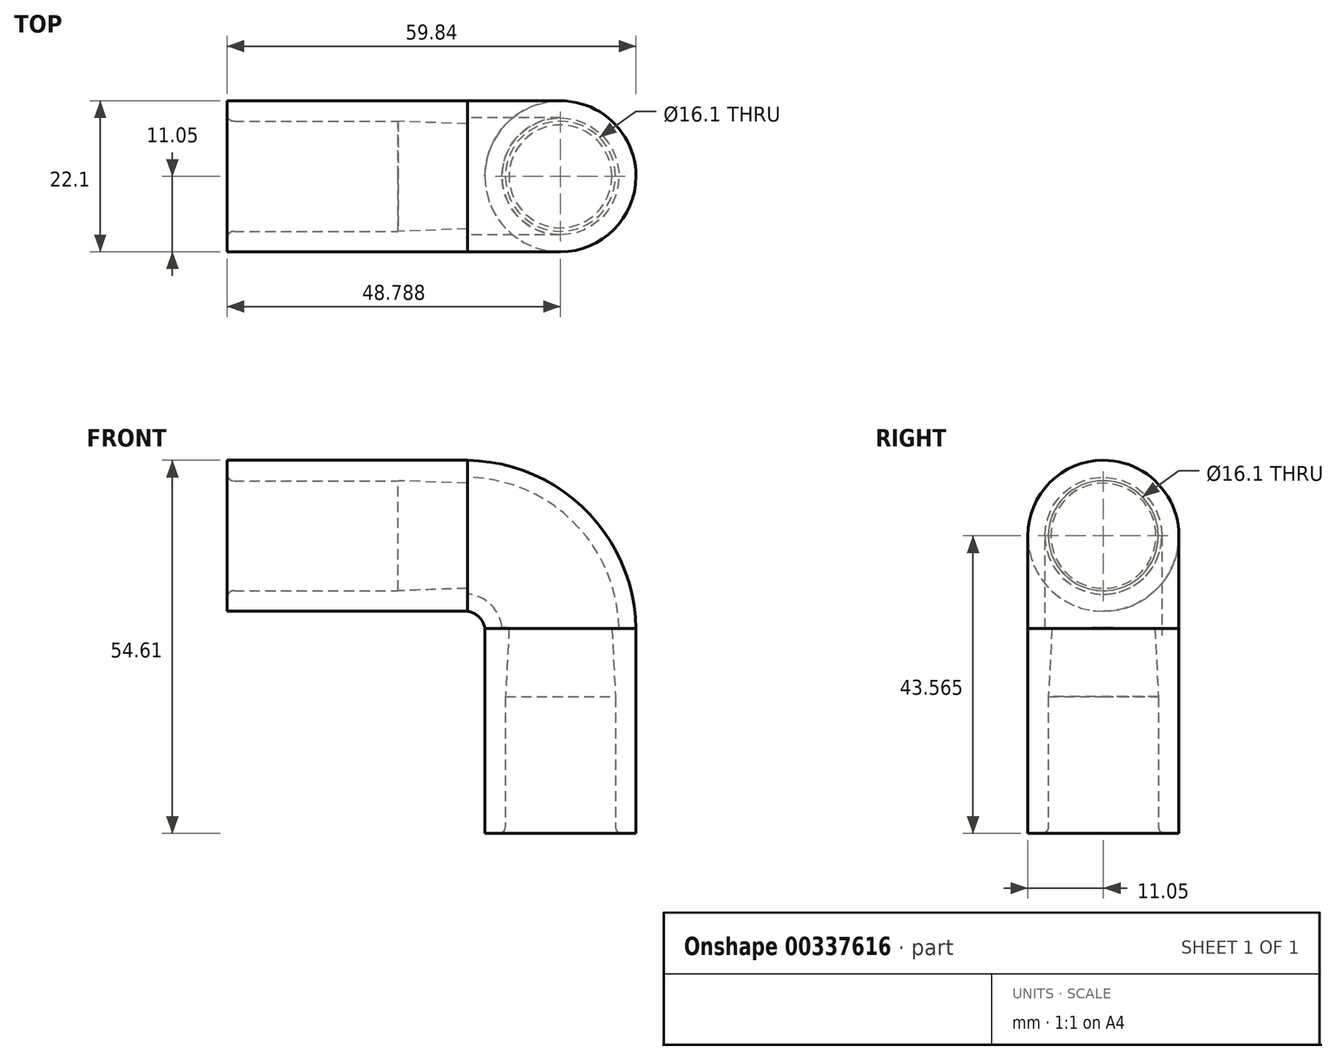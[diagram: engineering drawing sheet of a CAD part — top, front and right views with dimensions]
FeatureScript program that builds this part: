
annotation { "Feature Type Name" : "Feature", "Feature Type Description" : "" }
export const myFeature = defineFeature(function(context is Context, id is Id, definition is map)
    precondition{}
    {
        {
            var Q0;
            Q0=qCreatedBy(makeId("Front.planeOp"),FACE);
            var sketch = newSketch(context, id + "F0", { "sketchPlane" : qUnion([Q0])});
            skLineSegment(sketch, "E0", {"start": v(-11.93, -0.1) * mm, "end": v(-16.93, -0.1) * mm});
            skLineSegment(sketch, "E1", {"start": v(18.23, 2.9) * mm, "end": v(-16.93, 2.9) * mm});
            skLineSegment(sketch, "E2", {"start": v(-16.93, 2.9) * mm, "end": v(-16.93, -0.1) * mm});
            skLineSegment(sketch, "E3", {"start": v(36.1, -8.15) * mm, "end": v(3.24, -8.15) * mm, "construction": true});
            skLineSegment(sketch, "E4", {"start": v(8.07, -0.1) * mm, "end": v(-11.93, -0.1) * mm});
            skLineSegment(sketch, "E5", {"start": v(18.23, 2.9) * mm, "end": v(18.23, -0.45) * mm});
            skLineSegment(sketch, "E6", {"start": v(18.23, -0.45) * mm, "end": v(8.07, -0.1) * mm});
            skSolve(sketch);
        }
        {
            var Q0;
            Q0=makeQuery(id+"F0.imprint","IMPRINT",FACE,{"disambiguationData":[TD([[makeQuery(id+"F0.imprint","IMPRINT",EDGE,{"derivedFrom":sQuery(id+"F0.wireOp",EDGE,"E0")}),-1.0]])]});
            var Q1;
            Q1=sQuery(id+"F0.wireOp",EDGE,"E3");
            revolve(context, id + "F1", {"entities" : qUnion([Q0]), "axis" : qUnion([Q1]), "revolveType" : RevolveType.FULL});
        }
        {
            var Q0;
            Q0=qCreatedBy(makeId("Front.planeOp"),FACE);
            var sketch = newSketch(context, id + "F2", { "sketchPlane" : qUnion([Q0])});
            skLineSegment(sketch, "E7.1.0", {"start": v(31.86, -50.27) * mm, "end": v(31.86, -17.42) * mm, "construction": true});
            skLineSegment(sketch, "E7.1.1", {"start": v(39.9, -51.71) * mm, "end": v(39.9, -31.71) * mm});
            skLineSegment(sketch, "E7.1.2", {"start": v(39.9, -31.71) * mm, "end": v(39.38, -21.71) * mm});
            skLineSegment(sketch, "E7.1.3", {"start": v(42.9, -51.71) * mm, "end": v(42.9, -21.71) * mm});
            skLineSegment(sketch, "E7.1.4", {"start": v(42.9, -21.71) * mm, "end": v(39.38, -21.71) * mm});
            skLineSegment(sketch, "E7.1.5", {"start": v(39.9, -51.71) * mm, "end": v(42.9, -51.71) * mm});
            skPoint(sketch, "E8.0.internal.snap0", {"position": v(41.15, -21.71) * mm});
            skSolve(sketch);
        }
        {
            var Q0;
            Q0 = qSketchRegion(id + "F2", true);
            var Q1;
            Q1=sQuery(id+"F2.wireOp",EDGE,"E7.1.0");
            revolve(context, id + "F3", {"entities" : qUnion([Q0]), "axis" : qUnion([Q1]), "revolveType" : RevolveType.FULL});
        }
        {
            var Q0;
            Q0=makeQuery(id+"F1.opRevolve","SWEPT_FACE",FACE,{"disambiguationData":[OSD([sQuery(id+"F0.wireOp",EDGE,"E5")])]});
            var sketch = newSketch(context, id + "F4", { "sketchPlane" : qUnion([Q0])});
            skCircle(sketch, "E9.0", {"center": v(0, -8.15) * mm, "radius": 11.05 * mm});
            skSolve(sketch);
        }
        {
            var Q0;
            Q0=makeQuery(id+"F3.opRevolve","SWEPT_FACE",FACE,{"disambiguationData":[OSD([sQuery(id+"F2.wireOp",EDGE,"E7.1.4")])]});
            var sketch = newSketch(context, id + "F5", { "sketchPlane" : qUnion([Q0])});
            skCircle(sketch, "E10.0", {"center": v(31.86, 0) * mm, "radius": 11.05 * mm});
            skSolve(sketch);
        }
        {
            var Q0;
            Q0=qCreatedBy(makeId("Front.planeOp"),FACE);
            var sketch = newSketch(context, id + "F6", { "sketchPlane" : qUnion([Q0])});
            skLineSegment(sketch, "E11.0", {"start": v(20.8, -21.71) * mm, "end": v(42.9, -21.71) * mm});
            skLineSegment(sketch, "E12.0", {"start": v(18.23, 2.9) * mm, "end": v(18.23, -19.2) * mm});
            skArc(sketch, "E13", {"start": v(20.8, -21.71) * mm, "mid": v(19.94, -20.03) * mm, "end": v(18.23, -19.2) * mm});
            skArc(sketch, "E14", {"start": v(42.9, -21.71) * mm, "mid": v(35.57, -4.4) * mm, "end": v(18.23, 2.9) * mm});
            skSolve(sketch);
        }
        {
            var Q0;
            Q0 = qSketchRegion(id + "F4", true);
            var Q1;
            Q1 = qSketchRegion(id + "F5", true);
            var Q2;
            Q2=sQuery(id+"F6.wireOp",EDGE,"E14");
            var Q3;
            Q3=sQuery(id+"F6.wireOp",EDGE,"E13");
            loft(context, id + "F7", {"operationType" : NewBodyOperationType.ADD, "addGuides" : true, "sheetProfilesArray" : [{ "sheetProfileEntities" : qUnion([Q0]) }, { "sheetProfileEntities" : qUnion([Q1]) }], "guidesArray" : [{ "guideEntities" : qUnion([Q2]), "guideDerivativeType" : LoftGuideDerivativeType.DEFAULT, "guideDerivativeMagnitude" : 1 }, { "guideEntities" : qUnion([Q3]), "guideDerivativeType" : LoftGuideDerivativeType.DEFAULT, "guideDerivativeMagnitude" : 1 }]});
        }
        {
            var Q0;
            Q0=makeQuery(id+"F7.opLoft","CAP_FACE",FACE,{"disambiguationData":[OSD([makeQuery(id+"F5.imprint","IMPRINT",FACE,{"disambiguationData":[TD([[makeQuery(id+"F5.imprint","IMPRINT",EDGE,{"derivedFrom":makeQuery(id+"F3.opRevolve","SWEPT_EDGE",EDGE,{"disambiguationData":[OSD([sQuery(id+"F2.wireOp",EDGE,"E7.1.2"),sQuery(id+"F2.wireOp",EDGE,"E7.1.4")])]})}),-1.0]])]})])],"isStart":true});
            var Q1;
            Q1=makeQuery(id+"F7.opLoft","CAP_FACE",FACE,{"disambiguationData":[OSD([makeQuery(id+"F4.imprint","IMPRINT",FACE,{"disambiguationData":[TD([[makeQuery(id+"F4.imprint","IMPRINT",EDGE,{"derivedFrom":makeQuery(id+"F1.opRevolve","SWEPT_EDGE",EDGE,{"disambiguationData":[OSD([sQuery(id+"F0.wireOp",EDGE,"E5"),sQuery(id+"F0.wireOp",EDGE,"E6")])]})}),1.0]])]})])],"isStart":true});
            shell(context, id + "F8", {"entities" : qUnion([Q0, Q1]), "thickness" : 2.5 * mm});
        }
        {
            var Q0;
            Q0=makeQuery(id+"F3.opRevolve","SWEPT_EDGE",EDGE,{"disambiguationData":[OSD([sQuery(id+"F2.wireOp",EDGE,"E7.1.1"),sQuery(id+"F2.wireOp",EDGE,"E7.1.5")])]});
            var Q1;
            Q1=makeQuery(id+"F1.opRevolve","SWEPT_EDGE",EDGE,{"disambiguationData":[OSD([sQuery(id+"F0.wireOp",EDGE,"E0"),sQuery(id+"F0.wireOp",EDGE,"E2")])]});
            fillet(context, id + "F9", {"entities" : qUnion([Q0, Q1]), "radius" : 1 * mm, "tangentPropagation" : true, "allowEdgeOverflow" : false});
        }
    });
